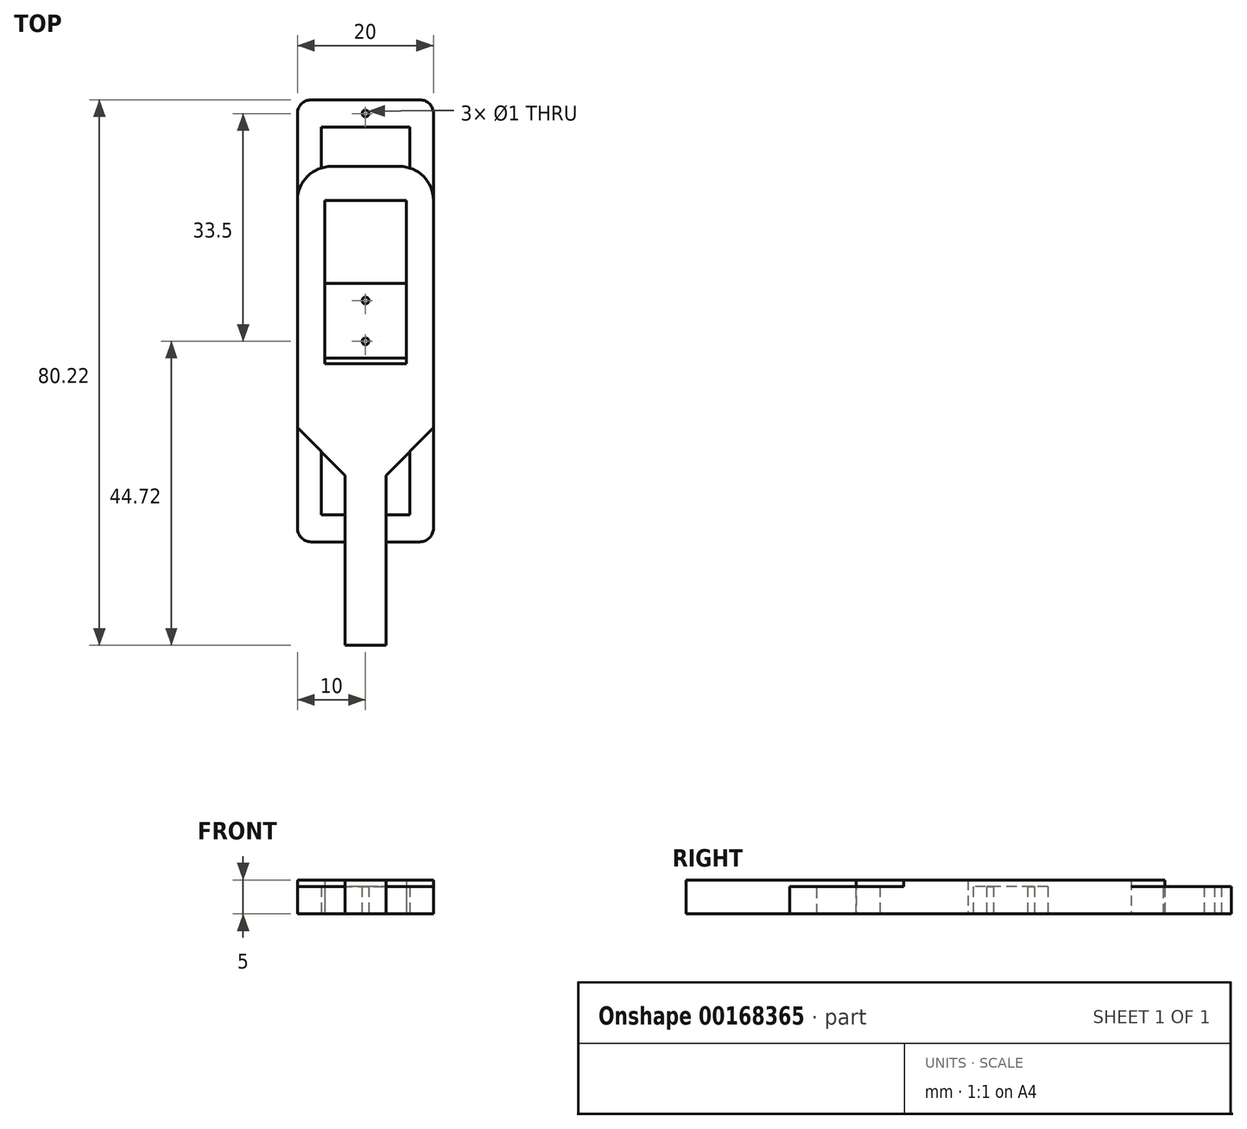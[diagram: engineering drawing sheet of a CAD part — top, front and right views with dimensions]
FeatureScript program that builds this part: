
annotation { "Feature Type Name" : "Feature", "Feature Type Description" : "" }
export const myFeature = defineFeature(function(context is Context, id is Id, definition is map)
    precondition{}
    {
        {
            var Q0;
            Q0=qCreatedBy(makeId("Top.planeOp"),FACE);
            var sketch = newSketch(context, id + "F0", { "sketchPlane" : qUnion([Q0])});
            skLineSegment(sketch, "E0.bottom", {"start": v(-10, -32.5) * mm, "end": v(10, -32.5) * mm});
            skLineSegment(sketch, "E0.top", {"start": v(-10, 32.5) * mm, "end": v(10, 32.5) * mm});
            skLineSegment(sketch, "E0.left", {"start": v(-10, -32.5) * mm, "end": v(-10, 32.5) * mm});
            skLineSegment(sketch, "E0.right", {"start": v(10, -32.5) * mm, "end": v(10, 32.5) * mm});
            skPoint(sketch, "E0.middle", {"position": v(0, 0) * mm});
            skLineSegment(sketch, "E1.bottom", {"start": v(6.5, 28.5) * mm, "end": v(-6.5, 28.5) * mm});
            skLineSegment(sketch, "E1.top", {"start": v(6.5, 5.5) * mm, "end": v(-6.5, 5.5) * mm});
            skLineSegment(sketch, "E1.left", {"start": v(6.5, 28.5) * mm, "end": v(6.5, 5.5) * mm});
            skLineSegment(sketch, "E1.right", {"start": v(-6.5, 28.5) * mm, "end": v(-6.5, 5.5) * mm});
            skPoint(sketch, "E1.middle", {"position": v(0, 17) * mm});
            skLineSegment(sketch, "E2.MirrorCS", {"start": v(6.5, -28.5) * mm, "end": v(-6.5, -28.5) * mm});
            skLineSegment(sketch, "E3.MirrorCS", {"start": v(-6.5, -28.5) * mm, "end": v(-6.5, -5.5) * mm});
            skLineSegment(sketch, "E4.MirrorCS", {"start": v(6.5, -28.5) * mm, "end": v(6.5, -5.5) * mm});
            skLineSegment(sketch, "E5.MirrorCS", {"start": v(6.5, -5.5) * mm, "end": v(-6.5, -5.5) * mm});
            skPoint(sketch, "E6", {"position": v(0, 30.5) * mm});
            skPoint(sketch, "E7", {"position": v(0, 3) * mm});
            skPoint(sketch, "E8", {"position": v(0, -3) * mm});
            skPoint(sketch, "E9", {"position": v(0, -30.5) * mm});
            skPoint(sketch, "E9.positionSnap0", {"position": v(0, -32.5) * mm});
            skCircle(sketch, "E10", {"center": v(0, 30.5) * mm, "radius": 0.5 * mm});
            skCircle(sketch, "E11", {"center": v(0, -30.5) * mm, "radius": 0.5 * mm});
            skCircle(sketch, "E12", {"center": v(0, 3) * mm, "radius": 0.5 * mm});
            skCircle(sketch, "E13", {"center": v(0, -3) * mm, "radius": 0.5 * mm});
            skSolve(sketch);
        }
        {
            var Q0;
            Q0 = qSketchRegion(id + "F0", true);
            extrude(context, id + "F1", {"entities" : qUnion([Q0]), "depth" : 4 * mm});
        }
        {
            var Q0;
            Q0=makeQuery(id+"F1.opExtrude","SWEPT_EDGE",EDGE,{"disambiguationData":[OSD([sQuery(id+"F0.wireOp",EDGE,"E0.bottom"),sQuery(id+"F0.wireOp",EDGE,"E0.right")])]});
            var Q1;
            Q1=makeQuery(id+"F1.opExtrude","SWEPT_EDGE",EDGE,{"disambiguationData":[OSD([sQuery(id+"F0.wireOp",EDGE,"E0.top"),sQuery(id+"F0.wireOp",EDGE,"E0.right")])]});
            var Q2;
            Q2=makeQuery(id+"F1.opExtrude","SWEPT_EDGE",EDGE,{"disambiguationData":[OSD([sQuery(id+"F0.wireOp",EDGE,"E0.bottom"),sQuery(id+"F0.wireOp",EDGE,"E0.left")])]});
            var Q3;
            Q3=makeQuery(id+"F1.opExtrude","SWEPT_EDGE",EDGE,{"disambiguationData":[OSD([sQuery(id+"F0.wireOp",EDGE,"E0.top"),sQuery(id+"F0.wireOp",EDGE,"E0.left")])]});
            fillet(context, id + "F2", {"entities" : qUnion([Q0, Q1, Q2, Q3]), "radius" : 2 * mm, "tangentPropagation" : true, "allowEdgeOverflow" : false});
        }
        {
            var Q0;
            Q0=qCreatedBy(makeId("Top.planeOp"),FACE);
            var sketch = newSketch(context, id + "F3", { "sketchPlane" : qUnion([Q0])});
            skLineSegment(sketch, "E14.bottom", {"start": v(-10, -22.72) * mm, "end": v(10, -22.72) * mm});
            skLineSegment(sketch, "E14.top", {"start": v(-10, 22.72) * mm, "end": v(10, 22.72) * mm});
            skLineSegment(sketch, "E14.left", {"start": v(-10, -22.72) * mm, "end": v(-10, 22.72) * mm});
            skLineSegment(sketch, "E14.right", {"start": v(10, -22.72) * mm, "end": v(10, 22.72) * mm});
            skPoint(sketch, "E14.middle", {"position": v(0, 0) * mm});
            skLineSegment(sketch, "E15.bottom", {"start": v(-6, -6.28) * mm, "end": v(6, -6.28) * mm});
            skLineSegment(sketch, "E15.top", {"start": v(-6, 17.72) * mm, "end": v(6, 17.72) * mm});
            skLineSegment(sketch, "E15.left", {"start": v(-6, -6.28) * mm, "end": v(-6, 17.72) * mm});
            skLineSegment(sketch, "E15.right", {"start": v(6, -6.28) * mm, "end": v(6, 17.72) * mm});
            skPoint(sketch, "E15.middle", {"position": v(0, 5.72) * mm});
            skPoint(sketch, "E16", {"position": v(0, 20.22) * mm});
            skPoint(sketch, "E16.positionSnap0", {"position": v(0, 22.72) * mm});
            skPoint(sketch, "E17", {"position": v(0, -22.72) * mm});
            skSolve(sketch);
        }
        {
            var Q0;
            Q0=makeQuery(id+"F3.imprint","IMPRINT",FACE,{"disambiguationData":[TD([[makeQuery(id+"F3.imprint","IMPRINT",EDGE,{"derivedFrom":sQuery(id+"F3.wireOp",EDGE,"E14.bottom")}),1.0]])]});
            extrude(context, id + "F4", {"entities" : qUnion([Q0]), "depth" : 5 * mm});
        }
        {
            var Q0;
            Q0=makeQuery(id+"F4.opExtrude","SWEPT_EDGE",EDGE,{"disambiguationData":[OSD([sQuery(id+"F3.wireOp",EDGE,"E14.bottom"),sQuery(id+"F3.wireOp",EDGE,"E14.left")])]});
            var Q1;
            Q1=makeQuery(id+"F4.opExtrude","SWEPT_EDGE",EDGE,{"disambiguationData":[OSD([sQuery(id+"F3.wireOp",EDGE,"E14.bottom"),sQuery(id+"F3.wireOp",EDGE,"E14.right")])]});
            chamfer(context, id + "F5", {"entities" : qUnion([Q0, Q1]), "width" : 7 * mm, "tangentPropagation" : true});
        }
        {
            var Q0;
            Q0=makeQuery(id+"F4.opExtrude","SWEPT_FACE",FACE,{"disambiguationData":[OSD([sQuery(id+"F3.wireOp",EDGE,"E14.bottom")])]});
            extrude(context, id + "F6", {"entities" : qUnion([Q0]), "operationType" : NewBodyOperationType.ADD, "depth" : 25 * mm});
        }
        {
            var Q0;
            Q0=makeQuery(id+"F4.opExtrude","SWEPT_EDGE",EDGE,{"disambiguationData":[OSD([sQuery(id+"F3.wireOp",EDGE,"E14.top"),sQuery(id+"F3.wireOp",EDGE,"E14.right")])]});
            var Q1;
            Q1=makeQuery(id+"F4.opExtrude","SWEPT_EDGE",EDGE,{"disambiguationData":[OSD([sQuery(id+"F3.wireOp",EDGE,"E14.top"),sQuery(id+"F3.wireOp",EDGE,"E14.left")])]});
            fillet(context, id + "F7", {"entities" : qUnion([Q0, Q1]), "radius" : 5 * mm, "tangentPropagation" : true, "allowEdgeOverflow" : false});
        }
    });
